# Revit family: Zumtobel PERLUCE Q
name_source: partatom
category: Lighting Fixtures
revit_build: Autodesk Revit 2016 (Build: 20150220_1215(x64)
units: mm (PartAtom-declared; Revit-internal decimal feet)

## family parameters
Cut with Voids When Loaded = No
Host = Face
Light Source = Yes
OmniClass Number = 23.80.70.11
OmniClass Title = Luminaries for Internal Lighting
Part Type = Normal
Room Calculation Point = No
Round Connector Dimension = Use Diameter
Shared = No

## types (5) — shared parameters
Body = Zumtobel_Metal_White
Color Filter = 16777215
Cover = Zumtobel_PMMA_White_Self_Illumination
Dimming Lamp Color Temperature Shift = <None>
Emit Shape Visible in Rendering = No
Height = 90 mm  [stored 0.295276 ft]
Manufacturer = Zumtobel Lighting
Tilt Angle = -90.00°
URL = http://www.zumtobel.com
Voltage = 230 V
zero-valued in all types: Default Elevation

## per-type parameters (varying)
| type | Apparent Load | Assembly Code | Description | Emit from Rectangle Length | Emit from Rectangle Width | Lamp | Length | Model | Photometric Web File | Width |
| PERLUCE O 2/18W TC-L Q310 Electronic | 33 VA | D5020210 | Square opal diffuser luminaires | 310 mm  [stored 1.01706 ft] | 310 mm  [stored 1.01706 ft] | TC-L | 310 mm  [stored 1.01706 ft] | 42921374 | 42921375_(STD).IES | 310 mm  [stored 1.01706 ft] |
| PERLUCE O 2/18W TC-L Q310 Dimmable | 42 VA | D5020210 | Square opal diffuser luminaires | 310 mm  [stored 1.01706 ft] | 310 mm  [stored 1.01706 ft] | TC-L | 310 mm  [stored 1.01706 ft] | 42921375 | 42921375_(STD).IES | 310 mm  [stored 1.01706 ft] |
| PERLUCE O 19W LED Q310 Dimmable | 19 VA | D5020200 | Square opal diffuser LED luminaires | 310 mm  [stored 1.01706 ft] | 310 mm  [stored 1.01706 ft] | LED | 310 mm  [stored 1.01706 ft] | 42181551 | 42181551_(STD).IES | 310 mm  [stored 1.01706 ft] |
| PERLUCE O 19W LED Q310 Electronic | 19 VA | D5020200 | Square opal diffuser LED luminaires | 310 mm  [stored 1.01706 ft] | 310 mm  [stored 1.01706 ft] | LED | 310 mm  [stored 1.01706 ft] | 42181552 | 42181551_(STD).IES | 310 mm  [stored 1.01706 ft] |
| PERLUCE O LED5200-840 Q620 LDE IP50 WH | 48 VA | D5020200 | Square opal diffuser LED luminaires | 620 mm  [stored 2.03412 ft] | 620 mm  [stored 2.03412 ft] | LED | 620 mm  [stored 2.03412 ft] | 42182932 | 42182932_(STD_LEO).IES | 620 mm  [stored 2.03412 ft] |

note: [stored X ft] marks values corroborated as IEEE doubles in the binary element streams (Revit-internal decimal feet)

## geometry (parser evidence)
native form markers: Sweep x3
no freeform markers — native parametric forms only
